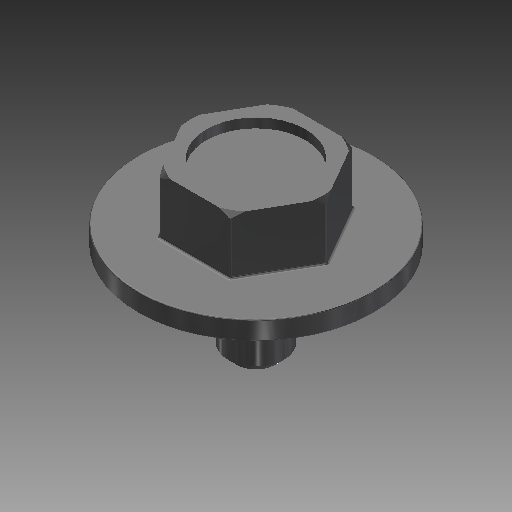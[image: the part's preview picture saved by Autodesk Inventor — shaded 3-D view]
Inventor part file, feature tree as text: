
AUTODESK INVENTOR PART (.ipt)
format: ipt  version: 2019 (Build 230136000, 136)  size: 187,904 bytes
history: native  units: mm
features: sketch x3, revolve x2, plane x2, extrude x1, fillet x1
ambient origin geometry x8: Origin, YZ Plane, XZ Plane, XY Plane, X Axis, Y Axis, Z Axis, Center Point
bodies: Solid1 (feature_tree)
feature tree (9):
  revolve  "Revolution1"  [1 undecoded]
  plane  "Work Plane1"
  extrude  "Extrusion1"  Depth=25.0mm
  fillet  "Fillet1"  Radius=10.5mm
  plane  "Work Plane2"
  revolve  "Revolution2"  [1 undecoded]
  sketch  "Sketch1"  dims[d0=1.0mm d1=1.0mm]
  sketch  "Sketch2"  dims[d2=6.0mm d3=25.0mm d4=10.5mm]
  sketch  "Sketch3"  dims[d5=2.0mm d7=10.0mm d10=5.0mm d11=90.0deg d12=0.125mm d15=8.0mm d16=13.0mm d17=10.5mm d18=10.0mm d19=0.0mm d20=0.25mm d21=0.0mm d22=0.5mm d23=0.5mm d26=7.5mm d27=8.0mm d28=90.0deg]
note: 2 required parameter values undecoded (feature->parameter linkage not recoverable at this tier; creation-order binding heuristic only, values carry confidence <= 0.55)
